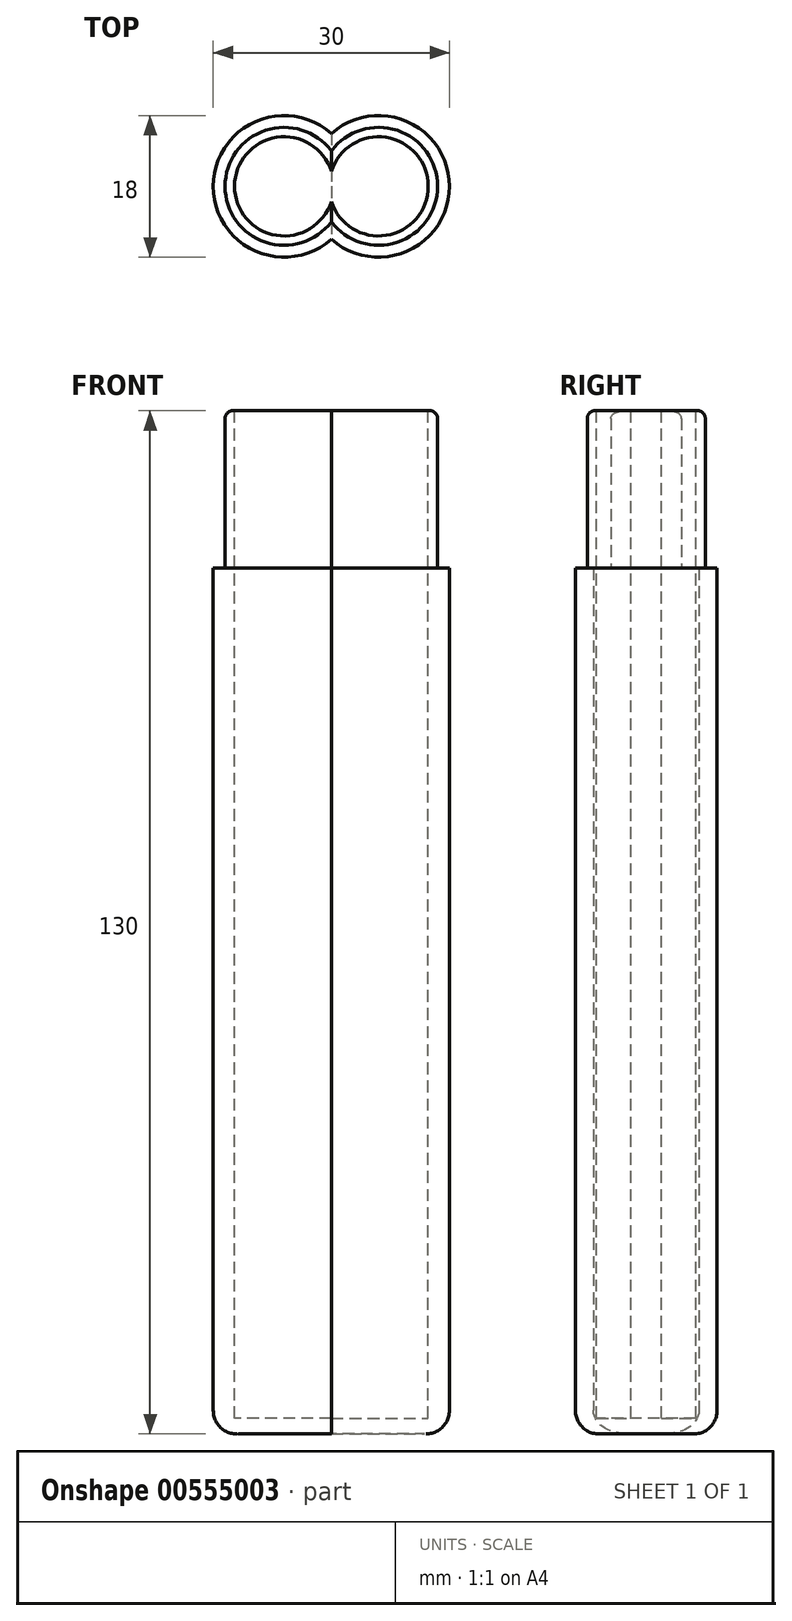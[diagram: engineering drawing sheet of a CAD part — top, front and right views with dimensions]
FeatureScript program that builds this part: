
annotation { "Feature Type Name" : "Feature", "Feature Type Description" : "" }
export const myFeature = defineFeature(function(context is Context, id is Id, definition is map)
    precondition{}
    {
        {
            var Q0;
            Q0=qCreatedBy(makeId("Top.planeOp"),FACE);
            var sketch = newSketch(context, id + "F0", { "sketchPlane" : qUnion([Q0])});
            skCircle(sketch, "E0", {"center": v(6, 0) * mm, "radius": 9 * mm});
            skCircle(sketch, "E1", {"center": v(-6, 0) * mm, "radius": 9 * mm});
            skSolve(sketch);
        }
        {
            var Q0;
            {var subQ0=sQuery(id+"F0.wireOp",EDGE,"E1");var subQ1=sQuery(id+"F0.wireOp",EDGE,"E0");var subQ2=makeQuery(id+"F0.imprint","INTERSECT",VERTEX,{"disambiguationData":[OD(0.0)],"derivedFrom":[subQ1,subQ0]});Q0=makeQuery(id+"F0.imprint","IMPRINT",FACE,{"disambiguationData":[TD([[makeQuery(id+"F0.imprint","IMPRINT",EDGE,{"disambiguationData":[TD([[subQ2,1.0]])],"derivedFrom":subQ1}),-1.0]])]});}
            var Q1;
            {var subQ0=sQuery(id+"F0.wireOp",EDGE,"E1");var subQ1=sQuery(id+"F0.wireOp",EDGE,"E0");var subQ2=makeQuery(id+"F0.imprint","INTERSECT",VERTEX,{"disambiguationData":[OD(0.0)],"derivedFrom":[subQ1,subQ0]});Q1=makeQuery(id+"F0.imprint","IMPRINT",FACE,{"disambiguationData":[TD([[makeQuery(id+"F0.imprint","IMPRINT",EDGE,{"disambiguationData":[TD([[subQ2,1.0]])],"derivedFrom":subQ1}),1.0]])]});}
            var Q2;
            {var subQ0=sQuery(id+"F0.wireOp",EDGE,"E1");var subQ1=sQuery(id+"F0.wireOp",EDGE,"E0");var subQ2=makeQuery(id+"F0.imprint","INTERSECT",VERTEX,{"disambiguationData":[OD(0.0)],"derivedFrom":[subQ1,subQ0]});Q2=makeQuery(id+"F0.imprint","IMPRINT",FACE,{"disambiguationData":[TD([[makeQuery(id+"F0.imprint","IMPRINT",EDGE,{"disambiguationData":[TD([[subQ2,-1.0]])],"derivedFrom":subQ1}),1.0]])]});}
            extrude(context, id + "F1", {"entities" : qUnion([Q0, Q1, Q2]), "depth" : 110 * mm, "offsetDistance" : 25 * mm});
        }
        {
            var Q0;
            Q0=makeQuery(id+"F1.opExtrude","CAP_FACE",FACE,{"disambiguationData":[OSD([sQuery(id+"F0.wireOp",EDGE,"E0"),sQuery(id+"F0.wireOp",EDGE,"E1")])],"isStart":false});
            var sketch = newSketch(context, id + "F2", { "sketchPlane" : qUnion([Q0])});
            skCircle(sketch, "E2", {"center": v(-6, 0) * mm, "radius": 7.5 * mm});
            skCircle(sketch, "E3", {"center": v(6, 0) * mm, "radius": 7.5 * mm});
            skSolve(sketch);
        }
        {
            var Q0;
            Q0 = qSketchRegion(id + "F2", true);
            extrude(context, id + "F3", {"entities" : qUnion([Q0]), "operationType" : NewBodyOperationType.ADD, "depth" : 20 * mm, "offsetDistance" : 25 * mm});
        }
        {
            var Q0;
            Q0=makeQuery(id+"F3.opExtrude","CAP_FACE",FACE,{"disambiguationData":[OSD([sQuery(id+"F2.wireOp",EDGE,"E2"),sQuery(id+"F2.wireOp",EDGE,"E3")])],"isStart":false});
            var sketch = newSketch(context, id + "F4", { "sketchPlane" : qUnion([Q0])});
            skCircle(sketch, "E4", {"center": v(6, 0) * mm, "radius": 6.3 * mm});
            skCircle(sketch, "E5", {"center": v(-6, 0) * mm, "radius": 6.3 * mm});
            skSolve(sketch);
        }
        {
            var Q0;
            Q0 = qSketchRegion(id + "F4", true);
            extrude(context, id + "F5", {"entities" : qUnion([Q0]), "operationType" : NewBodyOperationType.REMOVE, "oppositeDirection" : true, "depth" : 128 * mm, "offsetDistance" : 25 * mm});
        }
        {
            var Q0;
            Q0=makeQuery(id+"F3.opExtrude","CAP_EDGE",EDGE,{"disambiguationData":[OSD([sQuery(id+"F2.wireOp",EDGE,"E3")])],"isStart":false});
            var Q1;
            Q1=makeQuery(id+"F3.opExtrude","CAP_EDGE",EDGE,{"disambiguationData":[OSD([sQuery(id+"F2.wireOp",EDGE,"E2")])],"isStart":false});
            fillet(context, id + "F6", {"entities" : qUnion([Q0, Q1]), "radius" : 1 * mm, "tangentPropagation" : true, "allowEdgeOverflow" : false});
        }
        {
            var Q0;
            Q0=makeQuery(id+"F1.opExtrude","CAP_EDGE",EDGE,{"disambiguationData":[OSD([sQuery(id+"F0.wireOp",EDGE,"E1")])],"isStart":true});
            var Q1;
            Q1=makeQuery(id+"F1.opExtrude","CAP_EDGE",EDGE,{"disambiguationData":[OSD([sQuery(id+"F0.wireOp",EDGE,"E0")])],"isStart":true});
            fillet(context, id + "F7", {"entities" : qUnion([Q0, Q1]), "radius" : 3 * mm, "tangentPropagation" : true, "allowEdgeOverflow" : false});
        }
    });
